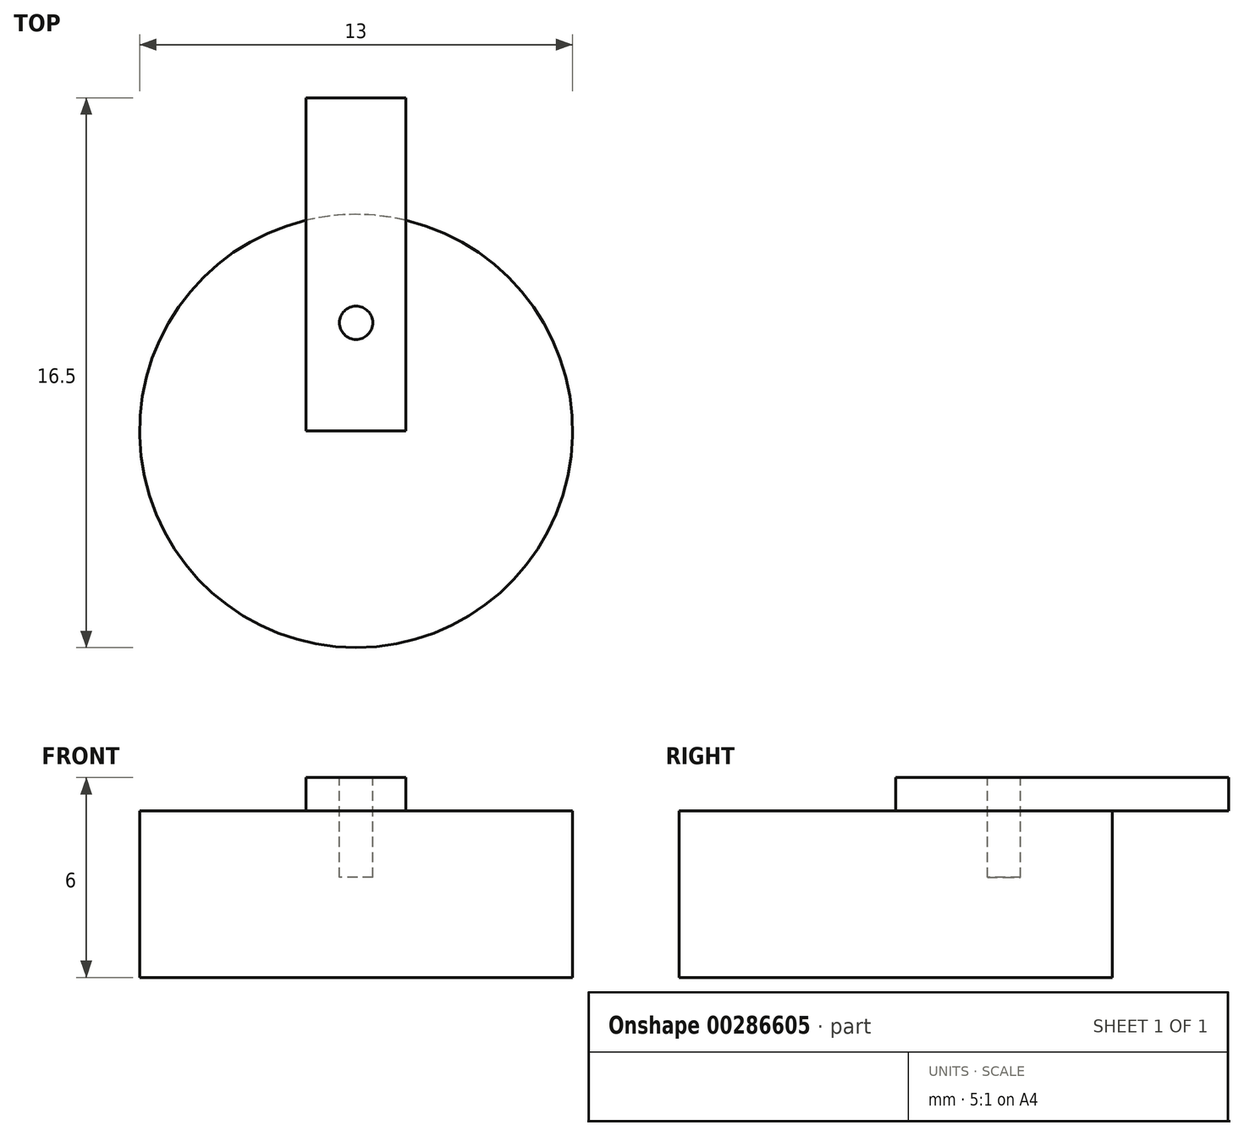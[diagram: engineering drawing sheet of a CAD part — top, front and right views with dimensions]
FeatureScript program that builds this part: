
annotation { "Feature Type Name" : "Feature", "Feature Type Description" : "" }
export const myFeature = defineFeature(function(context is Context, id is Id, definition is map)
    precondition{}
    {
        {
            var Q0;
            Q0=qCreatedBy(makeId("Top.planeOp"),FACE);
            var sketch = newSketch(context, id + "F0", { "sketchPlane" : qUnion([Q0])});
            skCircle(sketch, "E0", {"center": v(0, 0) * mm, "radius": 6.5 * mm});
            skSolve(sketch);
        }
        {
            var Q0;
            Q0=makeQuery(id+"F0.imprint","IMPRINT",FACE,{"disambiguationData":[TD([[makeQuery(id+"F0.imprint","IMPRINT",EDGE,{"derivedFrom":sQuery(id+"F0.wireOp",EDGE,"E0")}),1.0]])]});
            extrude(context, id + "F1", {"entities" : qUnion([Q0]), "depth" : 5 * mm});
        }
        {
            var Q0;
            Q0=makeQuery(id+"F1.opExtrude","CAP_FACE",FACE,{"disambiguationData":[OSD([sQuery(id+"F0.wireOp",EDGE,"E0")])],"isStart":false});
            var sketch = newSketch(context, id + "F2", { "sketchPlane" : qUnion([Q0])});
            skCircle(sketch, "E1", {"center": v(0, 3.25) * mm, "radius": 0.5 * mm});
            skSolve(sketch);
        }
        {
            var Q0;
            Q0=makeQuery(id+"F2.imprint","IMPRINT",FACE,{"disambiguationData":[TD([[makeQuery(id+"F2.imprint","IMPRINT",EDGE,{"derivedFrom":sQuery(id+"F2.wireOp",EDGE,"E1")}),1.0]])]});
            extrude(context, id + "F3", {"entities" : qUnion([Q0]), "operationType" : NewBodyOperationType.REMOVE, "oppositeDirection" : true, "depth" : 2 * mm});
        }
        {
            var Q0;
            Q0=makeQuery(id+"F1.opExtrude","CAP_FACE",FACE,{"disambiguationData":[OSD([sQuery(id+"F0.wireOp",EDGE,"E0")])],"isStart":false});
            var sketch = newSketch(context, id + "F4", { "sketchPlane" : qUnion([Q0])});
            skLineSegment(sketch, "E2.bottom", {"start": v(-1.5, 0) * mm, "end": v(1.5, 0) * mm});
            skLineSegment(sketch, "E2.top", {"start": v(-1.5, 10) * mm, "end": v(1.5, 10) * mm});
            skLineSegment(sketch, "E2.left", {"start": v(-1.5, 0) * mm, "end": v(-1.5, 10) * mm});
            skLineSegment(sketch, "E2.right", {"start": v(1.5, 0) * mm, "end": v(1.5, 10) * mm});
            skSolve(sketch);
        }
        {
            var Q0;
            {var subQ0=sQuery(id+"F4.wireOp",EDGE,"E2.top");Q0=makeQuery(id+"F4.imprint","IMPRINT",FACE,{"disambiguationData":[TD([[makeQuery(id+"F4.imprint","IMPRINT",EDGE,{"derivedFrom":subQ0}),-1.0]])]});}
            var Q1;
            {var subQ1=sQuery(id+"F4.wireOp",EDGE,"E2.bottom");Q1=makeQuery(id+"F4.imprint","IMPRINT",FACE,{"disambiguationData":[TD([[makeQuery(id+"F4.imprint","IMPRINT",EDGE,{"derivedFrom":subQ1}),1.0]])]});}
            extrude(context, id + "F5", {"entities" : qUnion([Q0, Q1]), "operationType" : NewBodyOperationType.ADD, "depth" : 1 * mm});
        }
    });
